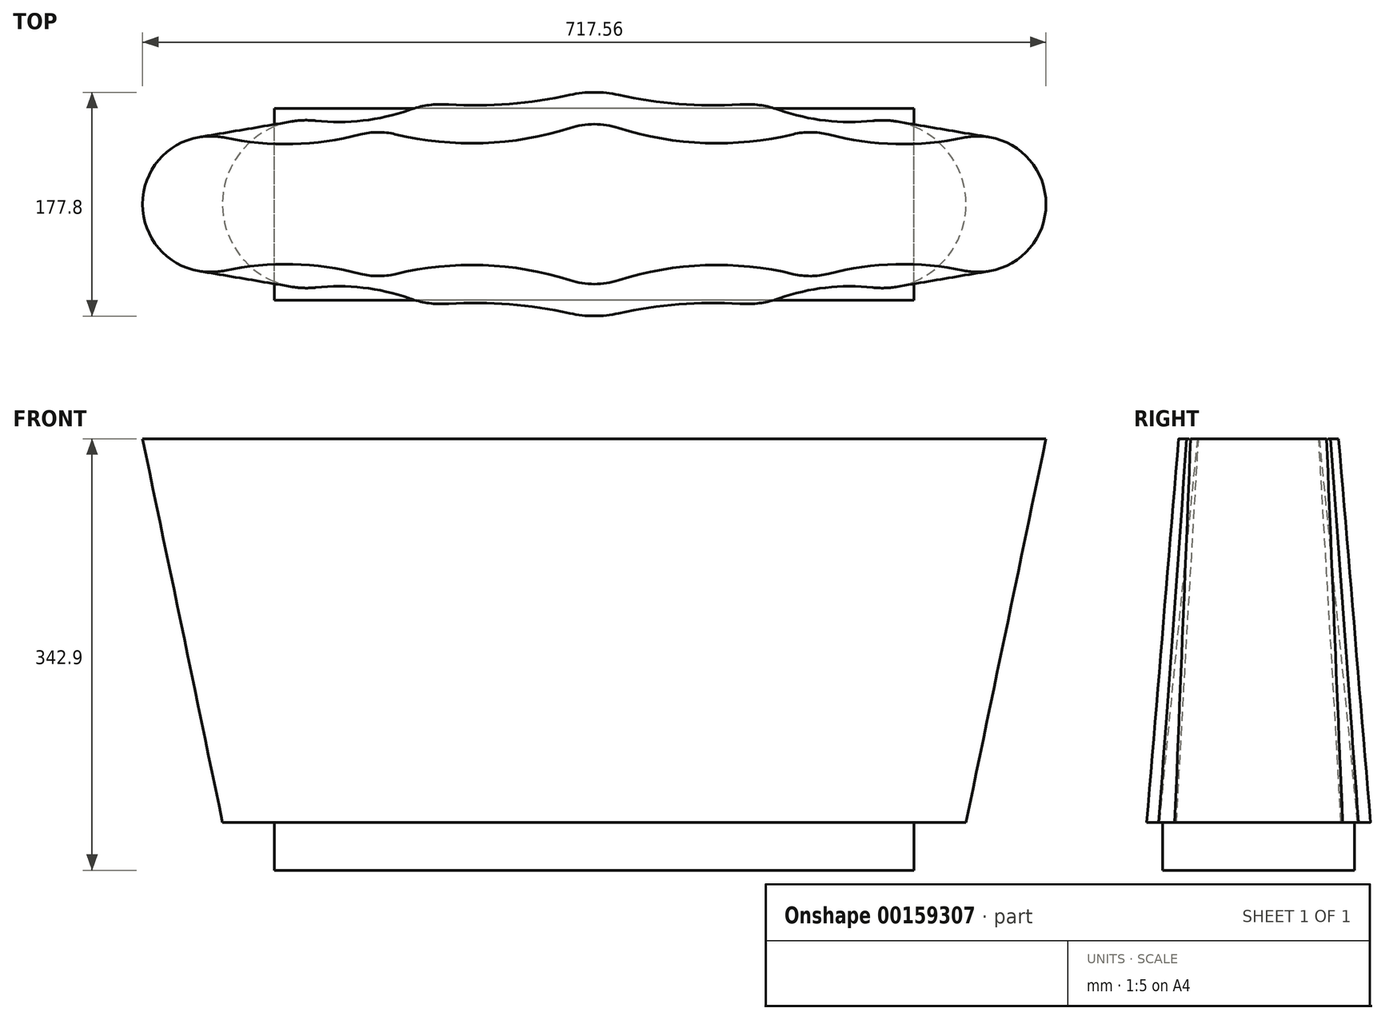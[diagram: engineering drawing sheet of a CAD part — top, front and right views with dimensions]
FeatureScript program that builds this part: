
annotation { "Feature Type Name" : "Feature", "Feature Type Description" : "" }
export const myFeature = defineFeature(function(context is Context, id is Id, definition is map)
    precondition{}
    {
        {
            var Q0;
            Q0=qCreatedBy(makeId("Top.planeOp"),FACE);
            var sketch = newSketch(context, id + "F0", { "sketchPlane" : qUnion([Q0])});
            skLineSegment(sketch, "E0.bottom", {"start": v(254, -76.2) * mm, "end": v(-254, -76.2) * mm});
            skLineSegment(sketch, "E0.top", {"start": v(254, 76.2) * mm, "end": v(-254, 76.2) * mm});
            skLineSegment(sketch, "E0.left", {"start": v(254, -76.2) * mm, "end": v(254, 76.2) * mm});
            skLineSegment(sketch, "E0.right", {"start": v(-254, -76.2) * mm, "end": v(-254, 76.2) * mm});
            skPoint(sketch, "E0.middle", {"position": v(0, 0) * mm});
            skSolve(sketch);
        }
        {
            var Q0;
            Q0=makeQuery(id+"F0.imprint","IMPRINT",FACE,{"disambiguationData":[TD([[makeQuery(id+"F0.imprint","IMPRINT",EDGE,{"derivedFrom":sQuery(id+"F0.wireOp",EDGE,"E0.bottom")}),-1.0]])]});
            extrude(context, id + "F1", {"entities" : qUnion([Q0]), "depth" : 38.1 * mm});
        }
        {
            var Q0;
            Q0=makeQuery(id+"F1.opExtrude","CAP_FACE",FACE,{"disambiguationData":[OSD([sQuery(id+"F0.wireOp",EDGE,"E0.bottom"),sQuery(id+"F0.wireOp",EDGE,"E0.top"),sQuery(id+"F0.wireOp",EDGE,"E0.left"),sQuery(id+"F0.wireOp",EDGE,"E0.right")])],"isStart":false});
            cPlane(context, id + "F2", {"entities" : qUnion([Q0]), "cplaneType" : CPlaneType.OFFSET, "offset" : 0 * mm, "width" : 152.4 * mm, "height" : 152.4 * mm});
        }
        {
            var Q0;
            Q0=qCreatedBy(id+"F2.planeOp",FACE);
            var sketch = newSketch(context, id + "F3", { "sketchPlane" : qUnion([Q0])});
            skArc(sketch, "E1", {"start": v(-19.34, -86.77) * mm, "mid": v(0, -88.9) * mm, "end": v(19.34, -86.77) * mm});
            skPoint(sketch, "E2.centerSnap0", {"position": v(254, 0) * mm});
            skPoint(sketch, "E3.MirrorP", {"position": v(-254, 0) * mm});
            skArc(sketch, "E4.MirrorC", {"start": v(-221.27, -66.27) * mm, "mid": v(-295.28, 0) * mm, "end": v(-221.27, 66.27) * mm});
            skArc(sketch, "E5.MirrorC", {"start": v(-147.12, 74.83) * mm, "mid": v(-131.62, 78.61) * mm, "end": v(-115.67, 79.22) * mm});
            skArc(sketch, "E6", {"start": v(-115.67, 79.22) * mm, "mid": v(-67.24, 79.6) * mm, "end": v(-19.34, 86.77) * mm});
            skArc(sketch, "E7", {"start": v(-221.27, 66.27) * mm, "mid": v(-183.71, 66.36) * mm, "end": v(-147.12, 74.83) * mm});
            skArc(sketch, "E8.MirrorCS", {"start": v(-115.67, -79.22) * mm, "mid": v(-67.24, -79.6) * mm, "end": v(-19.34, -86.77) * mm});
            skArc(sketch, "E9.MirrorCS", {"start": v(-221.27, -66.27) * mm, "mid": v(-183.71, -66.36) * mm, "end": v(-147.12, -74.83) * mm});
            skArc(sketch, "E10.trimOffspring", {"start": v(-115.67, -79.22) * mm, "mid": v(-131.62, -78.61) * mm, "end": v(-147.12, -74.83) * mm});
            skArc(sketch, "E11.MirrorCS", {"start": v(115.67, 79.22) * mm, "mid": v(67.24, 79.6) * mm, "end": v(19.34, 86.77) * mm});
            skArc(sketch, "E12.MirrorCS", {"start": v(147.12, 74.83) * mm, "mid": v(131.62, 78.61) * mm, "end": v(115.67, 79.22) * mm});
            skArc(sketch, "E13.MirrorCS", {"start": v(221.27, 66.27) * mm, "mid": v(183.71, 66.36) * mm, "end": v(147.12, 74.83) * mm});
            skArc(sketch, "E14.MirrorCS", {"start": v(221.27, -66.27) * mm, "mid": v(295.28, 0) * mm, "end": v(221.27, 66.27) * mm});
            skArc(sketch, "E15.MirrorCS", {"start": v(221.27, -66.27) * mm, "mid": v(183.71, -66.36) * mm, "end": v(147.12, -74.83) * mm});
            skArc(sketch, "E16.MirrorCS", {"start": v(115.67, -79.22) * mm, "mid": v(131.62, -78.61) * mm, "end": v(147.12, -74.83) * mm});
            skArc(sketch, "E17.MirrorCS", {"start": v(115.67, -79.22) * mm, "mid": v(67.24, -79.6) * mm, "end": v(19.34, -86.77) * mm});
            skArc(sketch, "E18.trimOffspring", {"start": v(19.34, 86.77) * mm, "mid": v(0, 88.9) * mm, "end": v(-19.34, 86.77) * mm});
            skSolve(sketch);
        }
        {
            var Q0;
            Q0=makeQuery(id+"F1.opExtrude","CAP_FACE",FACE,{"disambiguationData":[OSD([sQuery(id+"F0.wireOp",EDGE,"E0.bottom"),sQuery(id+"F0.wireOp",EDGE,"E0.top"),sQuery(id+"F0.wireOp",EDGE,"E0.left"),sQuery(id+"F0.wireOp",EDGE,"E0.right")])],"isStart":false});
            cPlane(context, id + "F4", {"entities" : qUnion([Q0]), "cplaneType" : CPlaneType.OFFSET, "offset" : 304.8 * mm, "width" : 152.4 * mm, "height" : 152.4 * mm});
        }
        {
            var Q0;
            Q0=qCreatedBy(id+"F4.planeOp",FACE);
            var sketch = newSketch(context, id + "F5", { "sketchPlane" : qUnion([Q0])});
            skArc(sketch, "E19", {"start": v(-19.26, -60.5) * mm, "mid": v(0, -63.5) * mm, "end": v(19.26, -60.5) * mm});
            skArc(sketch, "E20", {"start": v(-185.88, -55.3) * mm, "mid": v(-171.97, -57.15) * mm, "end": v(-158.04, -55.55) * mm});
            skArc(sketch, "E21", {"start": v(-293.6, 52.8) * mm, "mid": v(-358.78, 0) * mm, "end": v(-293.6, -52.8) * mm});
            skCircle(sketch, "E22.0", {"center": v(-120.65, 0) * mm, "radius": 79.38 * mm, "construction": true});
            skArc(sketch, "E23.0", {"start": v(-189.7, -54.16) * mm, "mid": v(-295.28, 0) * mm, "end": v(-189.7, 54.16) * mm, "construction": true});
            skArc(sketch, "E24", {"start": v(-293.6, 52.8) * mm, "mid": v(-239.6, 47.77) * mm, "end": v(-185.88, 55.3) * mm});
            skArc(sketch, "E25", {"start": v(-158.04, 55.55) * mm, "mid": v(-88.31, 48.52) * mm, "end": v(-19.26, 60.5) * mm});
            skArc(sketch, "E26.MirrorCS", {"start": v(-293.6, -52.8) * mm, "mid": v(-239.6, -47.77) * mm, "end": v(-185.88, -55.3) * mm});
            skArc(sketch, "E27.MirrorCS", {"start": v(-158.04, -55.55) * mm, "mid": v(-88.31, -48.52) * mm, "end": v(-19.26, -60.5) * mm});
            skArc(sketch, "E28.trimOffspring", {"start": v(-158.04, 55.55) * mm, "mid": v(-171.97, 57.15) * mm, "end": v(-185.88, 55.3) * mm});
            skArc(sketch, "E29.MirrorCS", {"start": v(158.04, 55.55) * mm, "mid": v(88.31, 48.52) * mm, "end": v(19.26, 60.5) * mm});
            skArc(sketch, "E30.MirrorCS", {"start": v(158.04, 55.55) * mm, "mid": v(171.97, 57.15) * mm, "end": v(185.88, 55.3) * mm});
            skArc(sketch, "E31.MirrorCS", {"start": v(293.6, 52.8) * mm, "mid": v(239.6, 47.77) * mm, "end": v(185.88, 55.3) * mm});
            skArc(sketch, "E32.MirrorCS", {"start": v(293.6, 52.8) * mm, "mid": v(358.78, 0) * mm, "end": v(293.6, -52.8) * mm});
            skArc(sketch, "E33.MirrorCS", {"start": v(293.6, -52.8) * mm, "mid": v(239.6, -47.77) * mm, "end": v(185.88, -55.3) * mm});
            skArc(sketch, "E34.MirrorCS", {"start": v(185.88, -55.3) * mm, "mid": v(171.97, -57.15) * mm, "end": v(158.04, -55.55) * mm});
            skArc(sketch, "E35.MirrorCS", {"start": v(158.04, -55.55) * mm, "mid": v(88.31, -48.52) * mm, "end": v(19.26, -60.5) * mm});
            skArc(sketch, "E36.trimOffspring", {"start": v(19.26, 60.5) * mm, "mid": v(0, 63.5) * mm, "end": v(-19.26, 60.5) * mm});
            skSolve(sketch);
        }
        {
            var Q1;
            Q1 = qSketchRegion(id + "F3", true);
            var Q2;
            Q2 = qSketchRegion(id + "F5", true);
            loft(context, id + "F6", {"operationType" : NewBodyOperationType.ADD, "sheetProfilesArray" : [{ "sheetProfileEntities" : qUnion([Q1]) }, { "sheetProfileEntities" : qUnion([Q2]) }]});
        }
    });
